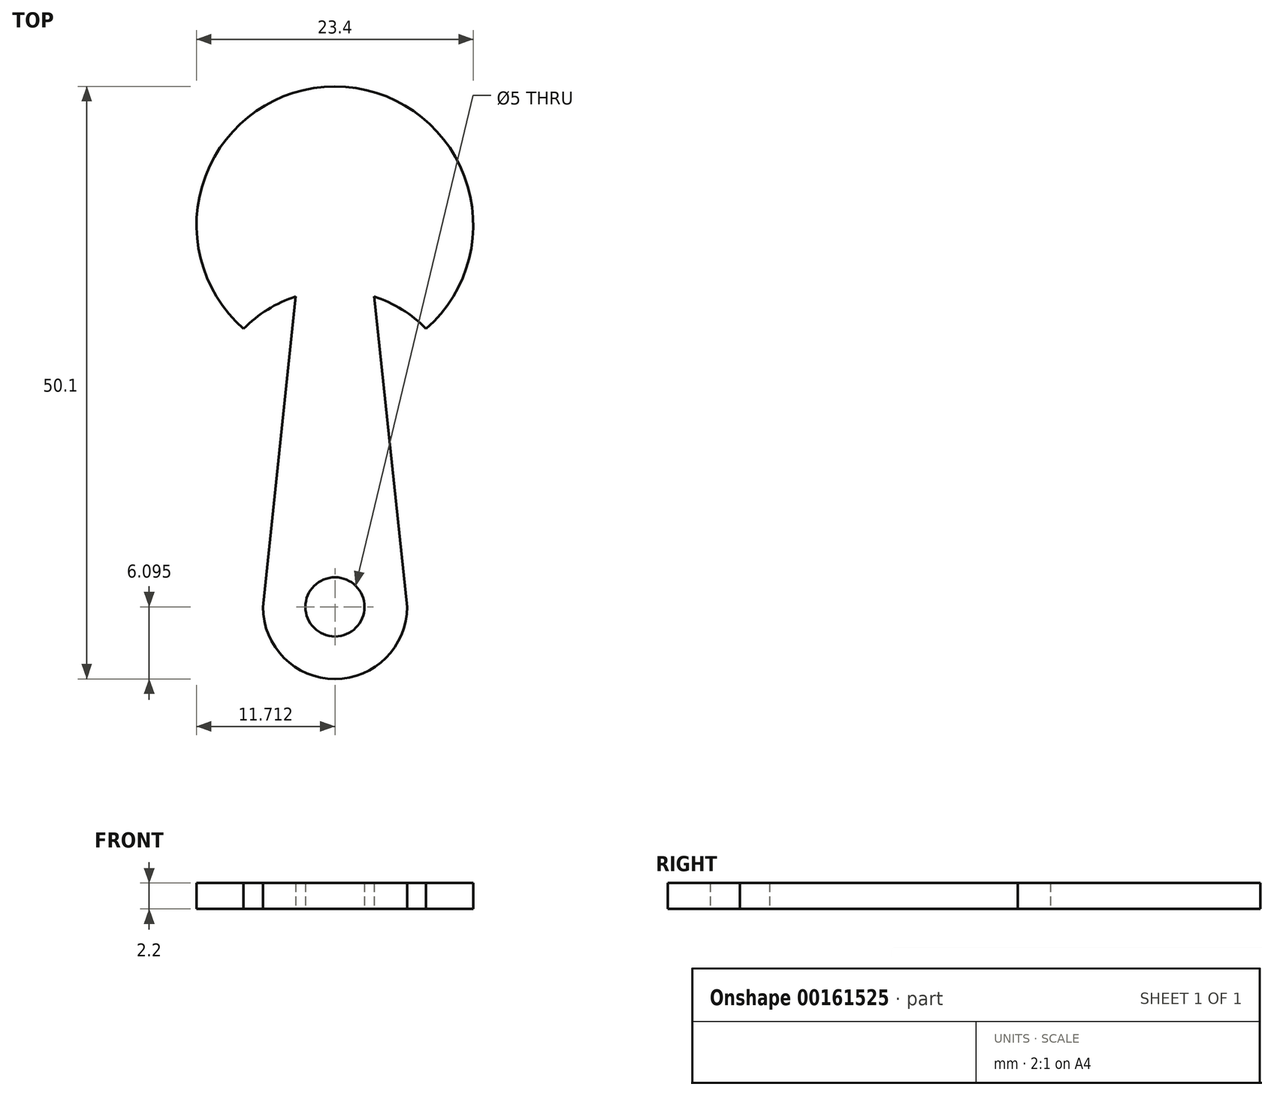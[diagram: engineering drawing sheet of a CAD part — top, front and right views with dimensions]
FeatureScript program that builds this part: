
annotation { "Feature Type Name" : "Feature", "Feature Type Description" : "" }
export const myFeature = defineFeature(function(context is Context, id is Id, definition is map)
    precondition{}
    {
        {
            var Q0;
            Q0=qCreatedBy(makeId("Top.planeOp"),FACE);
            var sketch = newSketch(context, id + "F0", { "sketchPlane" : qUnion([Q0])});
            skArc(sketch, "E0", {"start": v(0, 0) * mm, "mid": v(-7.72, 20.5) * mm, "end": v(-15.43, 0) * mm});
            skArc(sketch, "E1", {"start": v(0, 0) * mm, "mid": v(-2.03, 1.64) * mm, "end": v(-4.4, 2.74) * mm});
            skArc(sketch, "E2", {"start": v(-11.02, 2.74) * mm, "mid": v(-13.4, 1.64) * mm, "end": v(-15.43, 0) * mm});
            skLineSegment(sketch, "E3", {"start": v(-11.02, 2.74) * mm, "end": v(-11.02, 2.74) * mm});
            skLineSegment(sketch, "E4", {"start": v(-1.61, -23.5) * mm, "end": v(-4.4, 2.74) * mm});
            skLineSegment(sketch, "E5", {"start": v(-11.02, 2.74) * mm, "end": v(-13.8, -23.5) * mm});
            skLineSegment(sketch, "E6", {"start": v(-4.4, 2.74) * mm, "end": v(-4.4, 2.74) * mm});
            skArc(sketch, "E7", {"start": v(-13.8, -23.5) * mm, "mid": v(-7.7, -29.6) * mm, "end": v(-1.61, -23.5) * mm});
            skCircle(sketch, "E8", {"center": v(-7.7, -23.5) * mm, "radius": 2.5 * mm});
            skSolve(sketch);
        }
        {
            var Q0;
            Q0=makeQuery(id+"F0.imprint","IMPRINT",FACE,{"disambiguationData":[TD([[makeQuery(id+"F0.imprint","IMPRINT",EDGE,{"derivedFrom":sQuery(id+"F0.wireOp",EDGE,"E0")}),1.0]])]});
            extrude(context, id + "F1", {"entities" : qUnion([Q0]), "depth" : 2.2 * mm});
        }
    });
